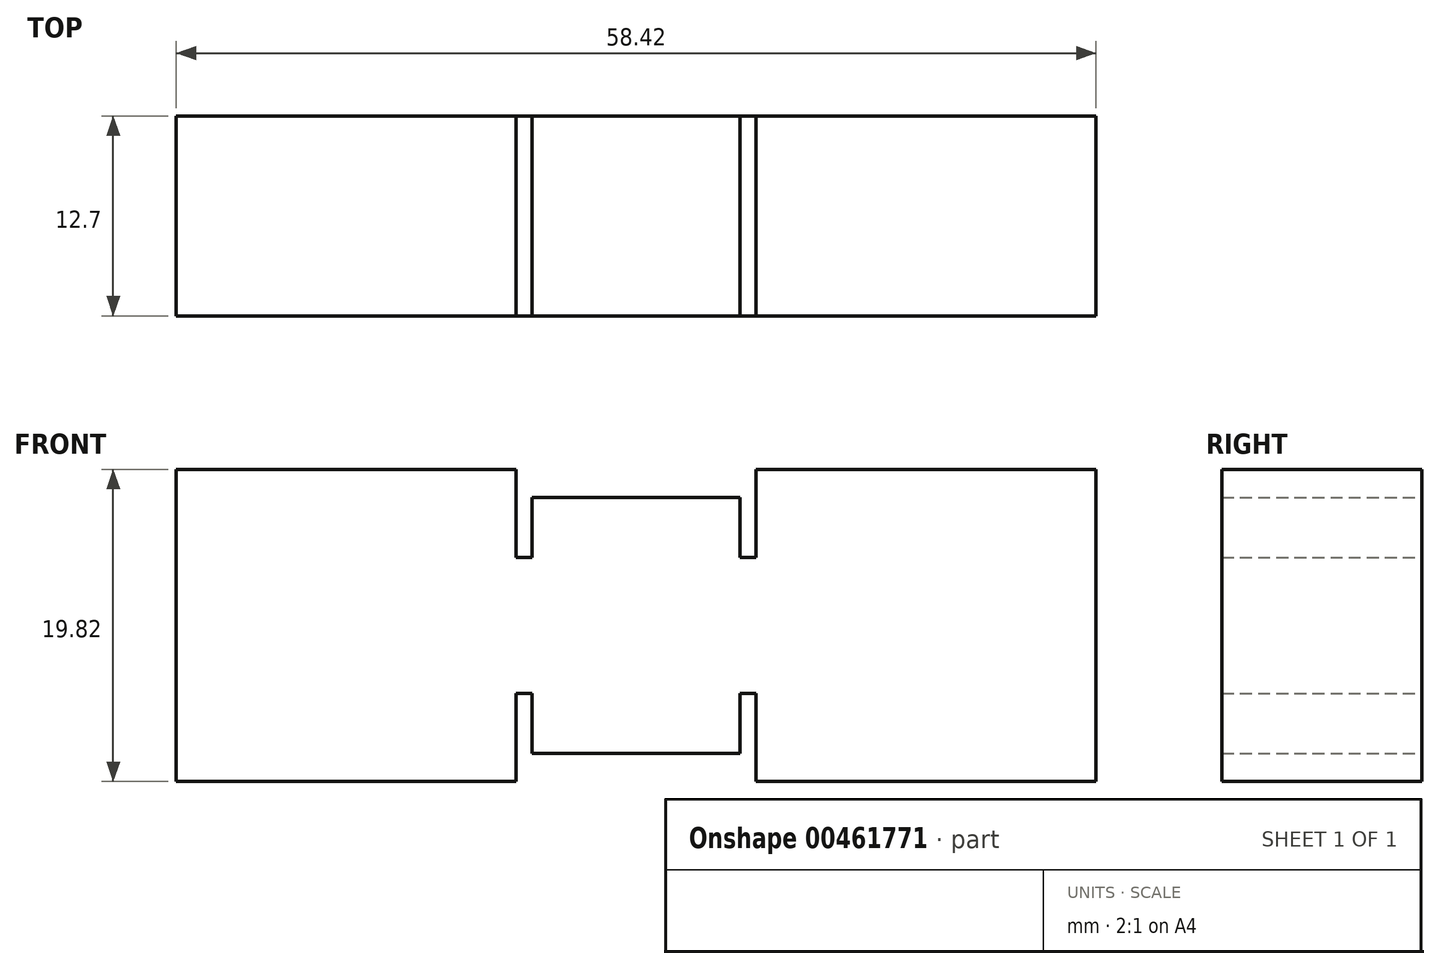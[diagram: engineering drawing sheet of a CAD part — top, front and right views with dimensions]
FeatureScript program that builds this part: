
annotation { "Feature Type Name" : "Feature", "Feature Type Description" : "" }
export const myFeature = defineFeature(function(context is Context, id is Id, definition is map)
    precondition{}
    {
        {
            var Q0;
            Q0=qCreatedBy(makeId("Front.planeOp"),FACE);
            var sketch = newSketch(context, id + "F0", { "sketchPlane" : qUnion([Q0])});
            skLineSegment(sketch, "E0", {"start": v(0, 0) * mm, "end": v(-29.21, 0) * mm});
            skLineSegment(sketch, "E1", {"start": v(0, 0) * mm, "end": v(0, 8.13) * mm});
            skLineSegment(sketch, "E2", {"start": v(-29.21, 0) * mm, "end": v(-29.21, 9.9) * mm});
            skLineSegment(sketch, "E3", {"start": v(-29.21, 9.9) * mm, "end": v(-7.62, 9.9) * mm});
            skLineSegment(sketch, "E4", {"start": v(-7.62, 9.9) * mm, "end": v(-7.62, 4.32) * mm});
            skLineSegment(sketch, "E5", {"start": v(-7.62, 4.32) * mm, "end": v(-6.6, 4.32) * mm});
            skLineSegment(sketch, "E6", {"start": v(-6.6, 4.32) * mm, "end": v(-6.6, 8.13) * mm});
            skLineSegment(sketch, "E7", {"start": v(-6.6, 8.13) * mm, "end": v(0, 8.13) * mm});
            skSolve(sketch);
        }
        {
            var Q0;
            Q0=makeQuery(id+"F0.imprint","IMPRINT",FACE,{"disambiguationData":[TD([[makeQuery(id+"F0.imprint","IMPRINT",EDGE,{"derivedFrom":sQuery(id+"F0.wireOp",EDGE,"E0")}),-1.0]])]});
            extrude(context, id + "F1", {"entities" : qUnion([Q0]), "depth" : 12.7 * mm});
        }
        {
            var Q0;
            Q0=makeQuery(id+"F1.opExtrude","SWEPT_BODY",BODY,{"disambiguationData":[OSD([sQuery(id+"F0.wireOp",EDGE,"E0"),sQuery(id+"F0.wireOp",EDGE,"E1"),sQuery(id+"F0.wireOp",EDGE,"E2"),sQuery(id+"F0.wireOp",EDGE,"E3"),sQuery(id+"F0.wireOp",EDGE,"E4"),sQuery(id+"F0.wireOp",EDGE,"E5"),sQuery(id+"F0.wireOp",EDGE,"E6"),sQuery(id+"F0.wireOp",EDGE,"E7")])]});
            var Q1;
            Q1=makeQuery(id+"F1.opExtrude","SWEPT_FACE",FACE,{"disambiguationData":[OSD([sQuery(id+"F0.wireOp",EDGE,"E0")])]});
            mirror(context, id + "F2", {"operationType" : NewBodyOperationType.ADD, "entities" : qUnion([Q0]), "mirrorPlane" : qUnion([Q1])});
        }
        {
            var Q0;
            Q0=makeQuery(id+"F1.opExtrude","SWEPT_BODY",BODY,{"disambiguationData":[OSD([sQuery(id+"F0.wireOp",EDGE,"E0"),sQuery(id+"F0.wireOp",EDGE,"E1"),sQuery(id+"F0.wireOp",EDGE,"E2"),sQuery(id+"F0.wireOp",EDGE,"E3"),sQuery(id+"F0.wireOp",EDGE,"E4"),sQuery(id+"F0.wireOp",EDGE,"E5"),sQuery(id+"F0.wireOp",EDGE,"E6"),sQuery(id+"F0.wireOp",EDGE,"E7")])]});
            var Q1;
            {var subQ0=makeQuery(id+"F1.opExtrude","SWEPT_FACE",FACE,{"disambiguationData":[OSD([sQuery(id+"F0.wireOp",EDGE,"E1")])]});Q1=makeQuery(id+"F2.boolean.opBoolean","MERGE",FACE,{"derivedFrom":[subQ0,makeQuery(id+"F2.opPattern","COPY",FACE,{"derivedFrom":subQ0,"instanceName":"1"})]});}
            mirror(context, id + "F3", {"operationType" : NewBodyOperationType.ADD, "entities" : qUnion([Q0]), "mirrorPlane" : qUnion([Q1])});
        }
    });
